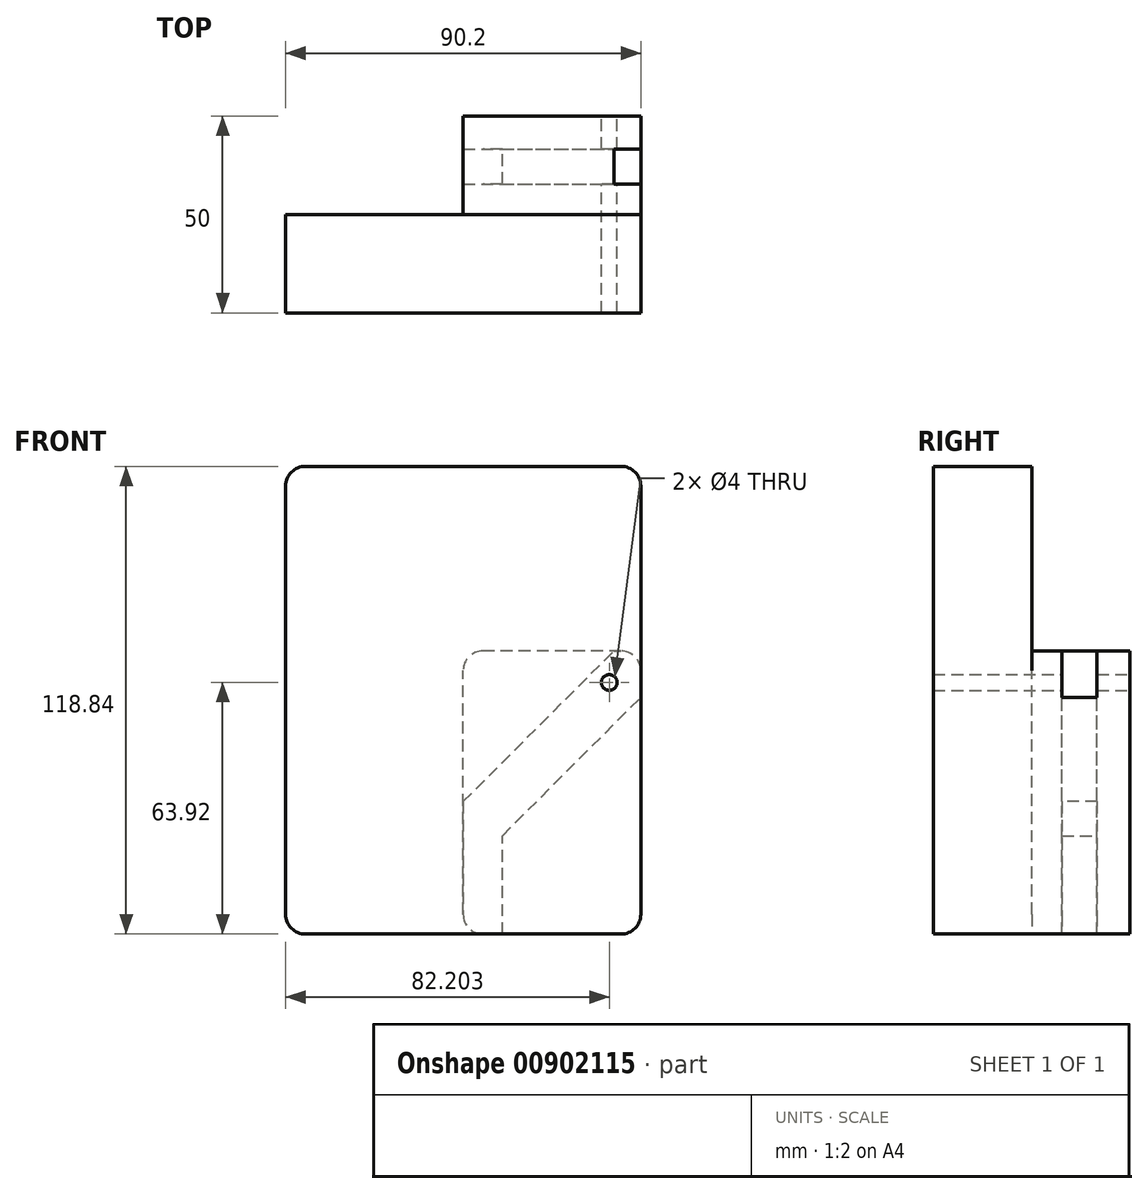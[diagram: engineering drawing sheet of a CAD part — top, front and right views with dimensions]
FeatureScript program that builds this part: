
annotation { "Feature Type Name" : "Feature", "Feature Type Description" : "" }
export const myFeature = defineFeature(function(context is Context, id is Id, definition is map)
    precondition{}
    {
        {
            var Q0;
            Q0=qCreatedBy(makeId("Front.planeOp"),FACE);
            var sketch = newSketch(context, id + "F0", { "sketchPlane" : qUnion([Q0])});
            skLineSegment(sketch, "E0.bottom", {"start": v(45.1, -46.92) * mm, "end": v(-45.1, -46.92) * mm});
            skLineSegment(sketch, "E0.top", {"start": v(45.1, 46.92) * mm, "end": v(-45.1, 46.92) * mm});
            skLineSegment(sketch, "E0.left", {"start": v(45.1, -46.92) * mm, "end": v(45.1, 46.92) * mm});
            skLineSegment(sketch, "E0.right", {"start": v(-45.1, -46.92) * mm, "end": v(-45.1, 46.92) * mm});
            skPoint(sketch, "E0.middle", {"position": v(0, 0) * mm});
            skSolve(sketch);
        }
        {
            var Q0;
            Q0=makeQuery(id+"F0.imprint","IMPRINT",FACE,{"disambiguationData":[TD([[makeQuery(id+"F0.imprint","IMPRINT",EDGE,{"derivedFrom":sQuery(id+"F0.wireOp",EDGE,"E0.bottom")}),-1.0]])]});
            extrude(context, id + "F1", {"entities" : qUnion([Q0]), "depth" : 25 * mm, "offsetDistance" : 25 * mm});
        }
        {
            var Q0;
            Q0=makeQuery(id+"F1.opExtrude","CAP_FACE",FACE,{"disambiguationData":[OSD([sQuery(id+"F0.wireOp",EDGE,"E0.bottom"),sQuery(id+"F0.wireOp",EDGE,"E0.top"),sQuery(id+"F0.wireOp",EDGE,"E0.left"),sQuery(id+"F0.wireOp",EDGE,"E0.right")])],"isStart":true});
            var sketch = newSketch(context, id + "F2", { "sketchPlane" : qUnion([Q0])});
            skLineSegment(sketch, "E1.bottom", {"start": v(-45.1, -46.92) * mm, "end": v(0, -46.92) * mm});
            skLineSegment(sketch, "E1.top", {"start": v(-45.1, 0) * mm, "end": v(0, 0) * mm});
            skLineSegment(sketch, "E1.left", {"start": v(-45.1, -46.92) * mm, "end": v(-45.1, 0) * mm});
            skLineSegment(sketch, "E1.right", {"start": v(0, -46.92) * mm, "end": v(0, 0) * mm});
            skSolve(sketch);
        }
        {
            var Q0;
            Q0 = qSketchRegion(id + "F2", true);
            extrude(context, id + "F3", {"entities" : qUnion([Q0]), "operationType" : NewBodyOperationType.ADD, "depth" : 25 * mm, "offsetDistance" : 25 * mm});
        }
        {
            var Q0;
            Q0=makeQuery(id+"F3.opExtrude","CAP_FACE",FACE,{"disambiguationData":[OSD([sQuery(id+"F2.wireOp",EDGE,"E1.bottom"),sQuery(id+"F2.wireOp",EDGE,"E1.top"),sQuery(id+"F2.wireOp",EDGE,"E1.left"),sQuery(id+"F2.wireOp",EDGE,"E1.right")])],"isStart":false});
            extrude(context, id + "F4", {"entities" : qUnion([Q0]), "operationType" : NewBodyOperationType.ADD, "oppositeDirection" : true, "depth" : 25 * mm, "offsetDistance" : 25 * mm});
        }
        {
            var Q0;
            Q0=qCreatedBy(makeId("Right.planeOp"),FACE);
            var Q1;
            Q1=makeQuery(id+"F3.opExtrude","SWEPT_EDGE",EDGE,{"disambiguationData":[OSD([sQuery(id+"F0.wireOp",EDGE,"E0.left"),sQuery(id+"F2.wireOp",EDGE,"E1.top"),sQuery(id+"F2.wireOp",EDGE,"E1.left")])]});
            cPlane(context, id + "F5", {"entities" : qUnion([Q0, Q1]), "cplaneType" : CPlaneType.LINE_ANGLE, "offset" : 25 * mm, "angle" : 45 * degree, "width" : 150 * mm, "height" : 150 * mm});
        }
        {
            var Q0;
            Q0=qCreatedBy(id+"F5.planeOp",FACE);
            var sketch = newSketch(context, id + "F6", { "sketchPlane" : qUnion([Q0])});
            skLineSegment(sketch, "E2.bottom", {"start": v(-16.62, -27.06) * mm, "end": v(-7.7, -27.06) * mm});
            skLineSegment(sketch, "E2.top", {"start": v(-16.62, -40.22) * mm, "end": v(-7.7, -40.22) * mm});
            skLineSegment(sketch, "E2.left", {"start": v(-16.62, -27.06) * mm, "end": v(-16.62, -40.22) * mm});
            skLineSegment(sketch, "E2.right", {"start": v(-7.7, -27.06) * mm, "end": v(-7.7, -40.22) * mm});
            skSolve(sketch);
        }
        {
            var Q0;
            Q0=makeQuery(id+"F6.imprint","IMPRINT",FACE,{"disambiguationData":[TD([[makeQuery(id+"F6.imprint","IMPRINT",EDGE,{"derivedFrom":sQuery(id+"F6.wireOp",EDGE,"E2.bottom")}),-1.0]])]});
            extrude(context, id + "F7", {"entities" : qUnion([Q0]), "operationType" : NewBodyOperationType.REMOVE, "endBound" : BoundingType.THROUGH_ALL, "depth" : 25 * mm, "offsetDistance" : 25 * mm});
        }
        {
            var Q0;
            Q0=makeQuery(id+"F3.boolean.opBoolean","MERGE",FACE,{"derivedFrom":[makeQuery(id+"F1.opExtrude","SWEPT_FACE",FACE,{"disambiguationData":[OSD([sQuery(id+"F0.wireOp",EDGE,"E0.bottom")])]}),makeQuery(id+"F3.opExtrude","SWEPT_FACE",FACE,{"disambiguationData":[OSD([sQuery(id+"F2.wireOp",EDGE,"E1.bottom")])]})]});
            var sketch = newSketch(context, id + "F8", { "sketchPlane" : qUnion([Q0])});
            skSolve(sketch);
        }
        {
            var Q0;
            {var subQ0=sQuery(id+"F0.wireOp",EDGE,"E0.bottom");Q0=makeQuery(id+"F8.imprint","IMPRINT",FACE,{"disambiguationData":[TD([[makeQuery(id+"F8.imprint","IMPRINT",EDGE,{"derivedFrom":makeQuery(id+"F1.opExtrude","CAP_EDGE",EDGE,{"disambiguationData":[OSD([subQ0])],"isStart":false})}),1.0]])]});}
            extrude(context, id + "F9", {"entities" : qUnion([Q0]), "operationType" : NewBodyOperationType.ADD, "depth" : 25 * mm, "offsetDistance" : 25 * mm});
        }
        {
            var Q0;
            {var subQ0=sQuery(id+"F2.wireOp",EDGE,"E1.right");var subQ1=sQuery(id+"F2.wireOp",EDGE,"E1.bottom");var subQ2=sQuery(id+"F0.wireOp",EDGE,"E0.bottom");Q0=makeQuery(id+"F9.opExtrude","CAP_EDGE",EDGE,{"disambiguationData":[OSD([subQ2,subQ1,subQ0]),TDD([makeQuery(id+"F8.imprint","IMPRINT",EDGE,{"derivedFrom":makeQuery(id+"F7.boolean.opBoolean","SPLIT",EDGE,{"disambiguationData":[TD([makeQuery(id+"F7.opExtrude","SWEPT_FACE",FACE,{"disambiguationData":[OSD([sQuery(id+"F6.wireOp",EDGE,"E2.right")])]})])],"derivedFrom":makeQuery(id+"F3.opExtrude","SWEPT_EDGE",EDGE,{"disambiguationData":[OSD([subQ2,subQ1,subQ0])]})})})])],"isStart":false});}
            var Q1;
            {var subQ0=sQuery(id+"F2.wireOp",EDGE,"E1.right");var subQ1=sQuery(id+"F2.wireOp",EDGE,"E1.bottom");var subQ2=sQuery(id+"F0.wireOp",EDGE,"E0.bottom");Q1=makeQuery(id+"F9.opExtrude","CAP_EDGE",EDGE,{"disambiguationData":[OSD([subQ2,subQ1,subQ0]),TDD([makeQuery(id+"F8.imprint","IMPRINT",EDGE,{"derivedFrom":makeQuery(id+"F7.boolean.opBoolean","SPLIT",EDGE,{"disambiguationData":[TD([makeQuery(id+"F7.opExtrude","SWEPT_FACE",FACE,{"disambiguationData":[OSD([sQuery(id+"F6.wireOp",EDGE,"E2.left")])]})])],"derivedFrom":makeQuery(id+"F3.opExtrude","SWEPT_EDGE",EDGE,{"disambiguationData":[OSD([subQ2,subQ1,subQ0])]})})})])],"isStart":false});}
            var Q2;
            Q2=makeQuery(id+"F3.opExtrude","SWEPT_EDGE",EDGE,{"disambiguationData":[OSD([sQuery(id+"F2.wireOp",EDGE,"E1.top"),sQuery(id+"F2.wireOp",EDGE,"E1.right")])]});
            var Q3;
            Q3=makeQuery(id+"F9.opExtrude","CAP_EDGE",EDGE,{"disambiguationData":[OSD([sQuery(id+"F0.wireOp",EDGE,"E0.bottom"),sQuery(id+"F0.wireOp",EDGE,"E0.right")])],"isStart":false});
            var Q4;
            Q4=makeQuery(id+"F9.opExtrude","CAP_EDGE",EDGE,{"disambiguationData":[OSD([sQuery(id+"F0.wireOp",EDGE,"E0.bottom"),sQuery(id+"F0.wireOp",EDGE,"E0.left"),sQuery(id+"F2.wireOp",EDGE,"E1.bottom"),sQuery(id+"F2.wireOp",EDGE,"E1.left")])],"isStart":false});
            var Q5;
            Q5=makeQuery(id+"F1.opExtrude","SWEPT_EDGE",EDGE,{"disambiguationData":[OSD([sQuery(id+"F0.wireOp",EDGE,"E0.top"),sQuery(id+"F0.wireOp",EDGE,"E0.right")])]});
            var Q6;
            Q6=makeQuery(id+"F1.opExtrude","SWEPT_EDGE",EDGE,{"disambiguationData":[OSD([sQuery(id+"F0.wireOp",EDGE,"E0.top"),sQuery(id+"F0.wireOp",EDGE,"E0.left")])]});
            var Q7;
            {var subQ0=sQuery(id+"F2.wireOp",EDGE,"E1.left");var subQ1=sQuery(id+"F2.wireOp",EDGE,"E1.top");var subQ2=sQuery(id+"F0.wireOp",EDGE,"E0.left");Q7=makeQuery(id+"F7.boolean.opBoolean","SPLIT",EDGE,{"disambiguationData":[TD([makeQuery(id+"F7.opExtrude","SWEPT_FACE",FACE,{"disambiguationData":[OSD([sQuery(id+"F6.wireOp",EDGE,"E2.left")])]})])],"derivedFrom":makeQuery(id+"F3.opExtrude","SWEPT_EDGE",EDGE,{"disambiguationData":[OSD([subQ2,subQ1,subQ0])]})});}
            var Q8;
            {var subQ0=sQuery(id+"F2.wireOp",EDGE,"E1.left");var subQ1=sQuery(id+"F0.wireOp",EDGE,"E0.left");var subQ2=sQuery(id+"F2.wireOp",EDGE,"E1.top");Q8=makeQuery(id+"F7.boolean.opBoolean","SPLIT",EDGE,{"disambiguationData":[TD([makeQuery(id+"F7.opExtrude","SWEPT_FACE",FACE,{"disambiguationData":[OSD([sQuery(id+"F6.wireOp",EDGE,"E2.right")])]})])],"derivedFrom":makeQuery(id+"F3.opExtrude","SWEPT_EDGE",EDGE,{"disambiguationData":[OSD([subQ1,subQ2,subQ0])]})});}
            fillet(context, id + "F10", {"entities" : qUnion([Q0, Q1, Q2, Q3, Q4, Q5, Q6, Q7, Q8]), "radius" : 5 * mm, "tangentPropagation" : true, "allowEdgeOverflow" : false});
        }
        {
            var Q0;
            {var subQ0=sQuery(id+"F2.wireOp",EDGE,"E1.bottom");Q0=makeQuery(id+"F9.boolean.opBoolean","MERGE",FACE,{"derivedFrom":[makeQuery(id+"F3.opExtrude","CAP_FACE",FACE,{"disambiguationData":[OSD([subQ0,sQuery(id+"F2.wireOp",EDGE,"E1.top"),sQuery(id+"F2.wireOp",EDGE,"E1.left"),sQuery(id+"F2.wireOp",EDGE,"E1.right")])],"isStart":false}),makeQuery(id+"F9.opExtrude","SWEPT_FACE",FACE,{"disambiguationData":[OSD([subQ0])]})]});}
            var sketch = newSketch(context, id + "F11", { "sketchPlane" : qUnion([Q0])});
            skSolve(sketch);
        }
        {
            var Q0;
            {var subQ3=sQuery(id+"F2.wireOp",EDGE,"E1.top");Q0=makeQuery(id+"F11.imprint","IMPRINT",FACE,{"disambiguationData":[TD([[makeQuery(id+"F11.imprint","IMPRINT",EDGE,{"derivedFrom":makeQuery(id+"F3.opExtrude","CAP_EDGE",EDGE,{"disambiguationData":[OSD([subQ3])],"isStart":false})}),-1.0]])]});}
            var sketch = newSketch(context, id + "F12", { "sketchPlane" : qUnion([Q0])});
            skSolve(sketch);
        }
        {
            var Q0;
            {var subQ3=sQuery(id+"F2.wireOp",EDGE,"E1.top");Q0=makeQuery(id+"F12.imprint","IMPRINT",FACE,{"disambiguationData":[TD([[makeQuery(id+"F12.imprint","IMPRINT",EDGE,{"derivedFrom":makeQuery(id+"F11.imprint","IMPRINT",EDGE,{"derivedFrom":makeQuery(id+"F3.opExtrude","CAP_EDGE",EDGE,{"disambiguationData":[OSD([subQ3])],"isStart":false})})}),-1.0]])]});}
            var sketch = newSketch(context, id + "F13", { "sketchPlane" : qUnion([Q0])});
            skPoint(sketch, "E3", {"position": v(-37.1, -8) * mm});
            skSolve(sketch);
        }
        {
            var Q0;
            Q0=sQuery(id+"F13.wireOp",VERTEX,"E3");
            var Q1;
            Q1=makeQuery(id+"F1.opExtrude","SWEPT_BODY",BODY,{"disambiguationData":[OSD([sQuery(id+"F0.wireOp",EDGE,"E0.bottom"),sQuery(id+"F0.wireOp",EDGE,"E0.top"),sQuery(id+"F0.wireOp",EDGE,"E0.left"),sQuery(id+"F0.wireOp",EDGE,"E0.right")])]});
            hole(context, id + "F14", {"style" : HoleStyle.SIMPLE, "endStyle" : HoleEndStyle.THROUGH, "holeDiameter" : 4 * mm, "majorDiameter" : 5 * mm, "isTappedThrough" : true, "tappedDepth" : 12 * mm, "tapClearance" : 3, "locations" : qUnion([Q0]), "scope" : qUnion([Q1])});
        }
    });
